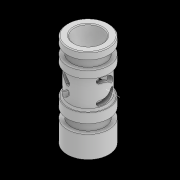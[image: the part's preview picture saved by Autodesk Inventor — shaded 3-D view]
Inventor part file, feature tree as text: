
AUTODESK INVENTOR PART (.ipt)
format: ipt  version: 2021 (Build 250183000, 183)  size: 453,120 bytes
history: native  units: mm
features: sketch x6, extrude x4, other x4, plane x3, chamfer x3, revolve x2, pattern_circular x2, fillet x1
ambient origin geometry x8: Origin, YZ Plane, XZ Plane, XY Plane, X Axis, Y Axis, Z Axis, Center Point
bodies: Solid1 (feature_tree)
feature tree (25):
  revolve  "Revolution1"  Angle=90.0deg
  plane  "Work Plane1"
  extrude  "Extrusion1"  Depth=2.0mm
  other  "Work Axis1"
  revolve  "Revolution2"  [1 undecoded]
  fillet  "Fillet1"  Radius=4.0mm
  pattern_circular  "Circular Pattern1"  Count=3 Angle=360.0deg
  plane  "Work Plane3"
  extrude  "Extrusion2"  Depth=2.5mm
  chamfer  "Chamfer3"  Angle=90.0deg  [1 undecoded]
  extrude  "Extrusion6"  Depth=0.1mm
  chamfer  "Chamfer5"  Distance=10.0mm
  other  "Work Axis2"
  chamfer  "Chamfer6"  Distance=0.25mm Angle=45.0deg
  plane  "Work Plane4"
  extrude  "Extrusion8"  Depth=9.0mm
  pattern_circular  "Circular Pattern3"  [2 undecoded]
  sketch  "Sketch2"  dims[d2=23.0mm d11=90.0deg]
  sketch  "Sketch3"  dims[d13=2.0mm d14=2.0mm]
  sketch  "Sketch4"  dims[d15=3.490659mm d16=3.490659mm d18=4.0mm]
  sketch  "Sketch5"  dims[d19=10.0mm d20=0.0mm]
  other  "Srf1"
  sketch  "Sketch10"  dims[d24=90.0deg]
  sketch  "Sketch13"  dims[d25=0.5mm d29=30.0mm d30=360.0deg d32=2.5mm d33=90.0deg d34=0.1mm d35=10.0mm d36=0.0mm d47=0.25mm d48=2.0mm d49=45.0deg d59=9.0mm d60=4.0mm d61=0.0mm d64=8.0mm d67=0.5mm d68=2.0mm d69=45.0deg d74=11.0mm d75=8.5mm d77=9.6mm d78=2.7mm d80=0.75mm d84=12.0mm d86=2.0mm d87=0.2mm d88=2.0mm d89=45.0deg d90=18.0mm d91=10.0mm d92=0.0mm d96=30.0mm d97=360.0deg d76=0.5mm d79=0.872665mm]
  other  "Unwrap1"
note: 4 required parameter values undecoded (feature->parameter linkage not recoverable at this tier; creation-order binding heuristic only, values carry confidence <= 0.55)